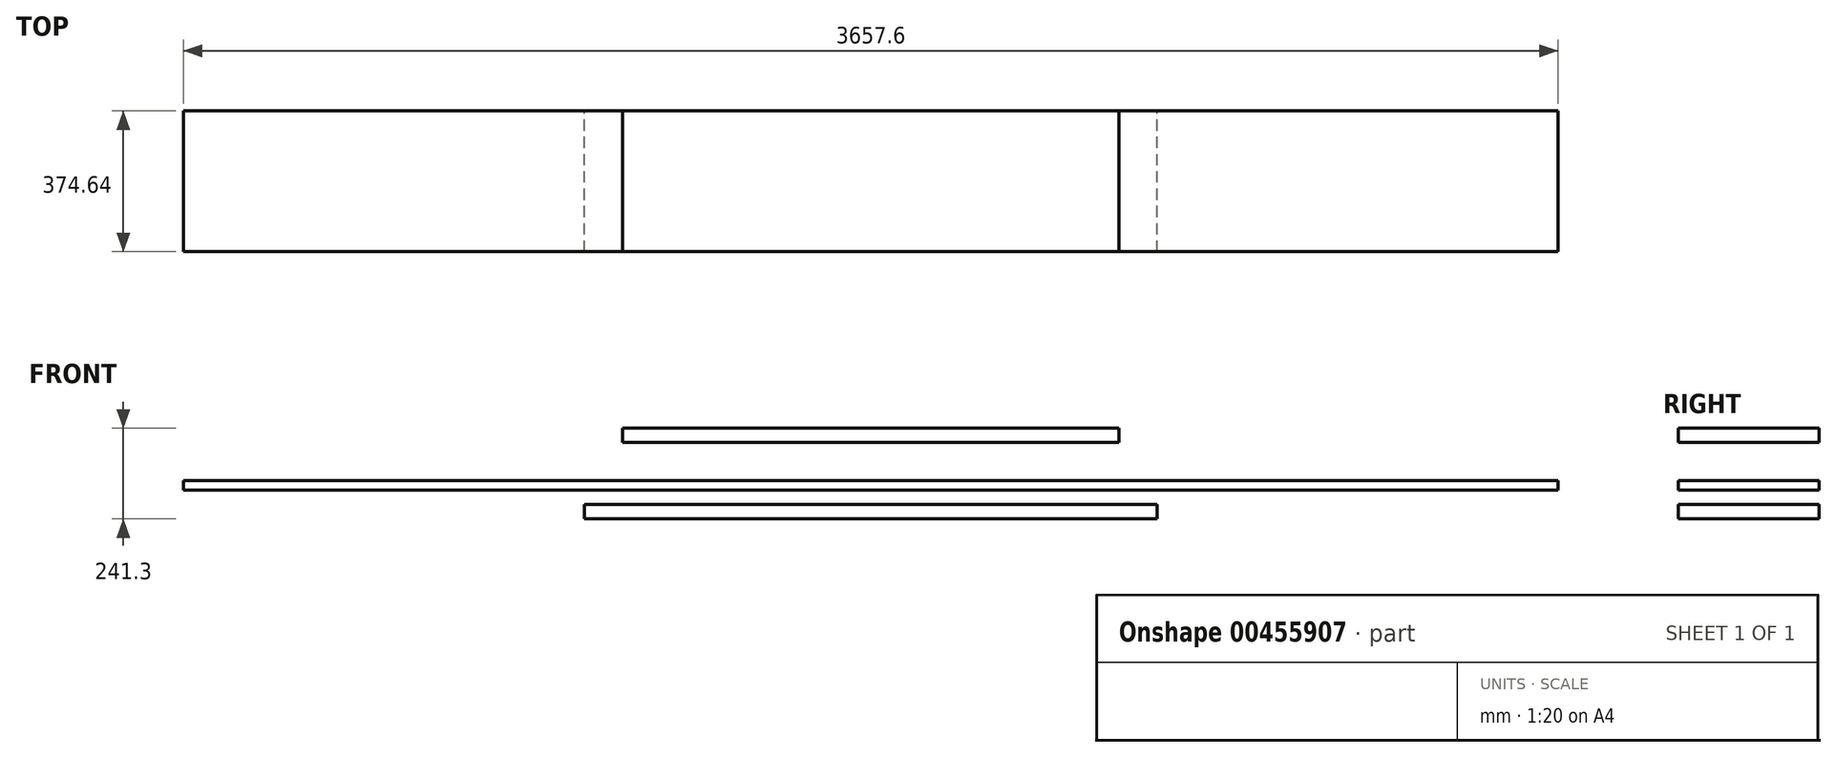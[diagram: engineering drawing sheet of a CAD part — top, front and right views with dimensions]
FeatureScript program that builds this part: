
annotation { "Feature Type Name" : "Feature", "Feature Type Description" : "" }
export const myFeature = defineFeature(function(context is Context, id is Id, definition is map)
    precondition{}
    {
        {
            var Q0;
            Q0=qCreatedBy(makeId("Top.planeOp"),FACE);
            var sketch = newSketch(context, id + "F0", { "sketchPlane" : qUnion([Q0])});
            skLineSegment(sketch, "E0.bottom", {"start": v(-762, -187.32) * mm, "end": v(762, -187.32) * mm});
            skLineSegment(sketch, "E0.top", {"start": v(-762, 187.32) * mm, "end": v(762, 187.32) * mm});
            skLineSegment(sketch, "E0.left", {"start": v(-762, -187.32) * mm, "end": v(-762, 187.32) * mm});
            skLineSegment(sketch, "E0.right", {"start": v(762, -187.32) * mm, "end": v(762, 187.32) * mm});
            skPoint(sketch, "E0.middle", {"position": v(0, 0) * mm});
            skSolve(sketch);
        }
        {
            var Q0;
            Q0 = qSketchRegion(id + "F0", true);
            extrude(context, id + "F1", {"entities" : qUnion([Q0]), "depth" : 38.1 * mm});
        }
        {
            var Q0;
            Q0=qCreatedBy(makeId("Top.planeOp"),FACE);
            cPlane(context, id + "F2", {"entities" : qUnion([Q0]), "cplaneType" : CPlaneType.OFFSET, "offset" : 76.2 * mm, "width" : 152.4 * mm, "height" : 152.4 * mm});
        }
        {
            var Q0;
            Q0=qCreatedBy(id+"F2.planeOp",FACE);
            var sketch = newSketch(context, id + "F3", { "sketchPlane" : qUnion([Q0])});
            skLineSegment(sketch, "E1.bottom", {"start": v(-1828.8, -187.32) * mm, "end": v(1828.8, -187.32) * mm});
            skLineSegment(sketch, "E1.top", {"start": v(-1828.8, 187.33) * mm, "end": v(1828.8, 187.33) * mm});
            skLineSegment(sketch, "E1.left", {"start": v(-1828.8, -187.32) * mm, "end": v(-1828.8, 187.33) * mm});
            skLineSegment(sketch, "E1.right", {"start": v(1828.8, -187.32) * mm, "end": v(1828.8, 187.33) * mm});
            skPoint(sketch, "E1.middle", {"position": v(0, 0) * mm});
            skSolve(sketch);
        }
        {
            var Q0;
            Q0=makeQuery(id+"F3.imprint","IMPRINT",FACE,{"disambiguationData":[TD([[makeQuery(id+"F3.imprint","IMPRINT",EDGE,{"derivedFrom":sQuery(id+"F3.wireOp",EDGE,"E1.bottom")}),1.0]])]});
            extrude(context, id + "F4", {"entities" : qUnion([Q0]), "operationType" : NewBodyOperationType.ADD, "depth" : 25.4 * mm});
        }
        {
            var Q0;
            Q0=qCreatedBy(id+"F2.planeOp",FACE);
            cPlane(context, id + "F5", {"entities" : qUnion([Q0]), "cplaneType" : CPlaneType.OFFSET, "offset" : 127 * mm, "width" : 152.4 * mm, "height" : 152.4 * mm});
        }
        {
            var Q0;
            Q0=qCreatedBy(id+"F5.planeOp",FACE);
            var sketch = newSketch(context, id + "F6", { "sketchPlane" : qUnion([Q0])});
            skLineSegment(sketch, "E2.bottom", {"start": v(-660.4, -187.32) * mm, "end": v(660.4, -187.32) * mm});
            skLineSegment(sketch, "E2.top", {"start": v(-660.4, 187.33) * mm, "end": v(660.4, 187.33) * mm});
            skLineSegment(sketch, "E2.left", {"start": v(-660.4, -187.32) * mm, "end": v(-660.4, 187.33) * mm});
            skLineSegment(sketch, "E2.right", {"start": v(660.4, -187.32) * mm, "end": v(660.4, 187.33) * mm});
            skPoint(sketch, "E2.middle", {"position": v(0, 0) * mm});
            skSolve(sketch);
        }
        {
            var Q0;
            Q0 = qSketchRegion(id + "F6", true);
            extrude(context, id + "F7", {"entities" : qUnion([Q0]), "depth" : 38.1 * mm});
        }
    });
